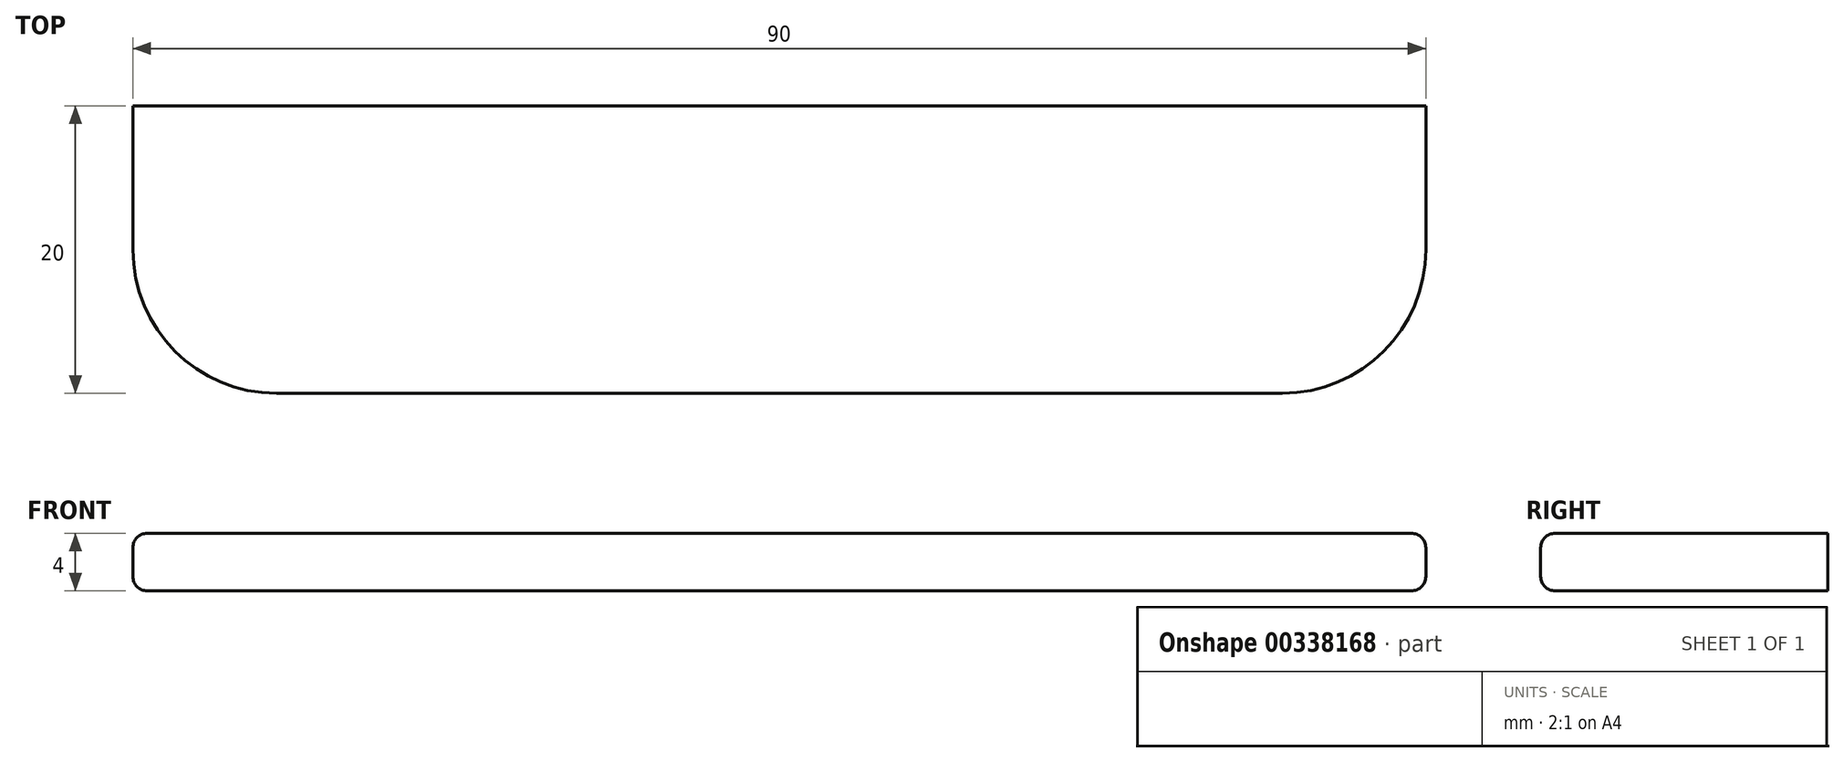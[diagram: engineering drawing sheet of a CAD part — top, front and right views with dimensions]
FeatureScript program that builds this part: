
annotation { "Feature Type Name" : "Feature", "Feature Type Description" : "" }
export const myFeature = defineFeature(function(context is Context, id is Id, definition is map)
    precondition{}
    {
        {
            var Q0;
            Q0=qCreatedBy(makeId("Top.planeOp"),FACE);
            var sketch = newSketch(context, id + "F0", { "sketchPlane" : qUnion([Q0])});
            skLineSegment(sketch, "E0.bottom", {"start": v(-45, 0) * mm, "end": v(45, 0) * mm});
            skLineSegment(sketch, "E0.top", {"start": v(-35, -20) * mm, "end": v(35, -20) * mm});
            skLineSegment(sketch, "E0.left", {"start": v(-45, 0) * mm, "end": v(-45, -10) * mm});
            skLineSegment(sketch, "E0.right", {"start": v(45, 0) * mm, "end": v(45, -10) * mm});
            skPoint(sketch, "E1.visualSharp", {"position": v(-45, -20) * mm});
            skArc(sketch, "E1.filletArc", {"start": v(-45, -10) * mm, "mid": v(-42.07, -17.07) * mm, "end": v(-35, -20) * mm});
            skPoint(sketch, "E2.visualSharp", {"position": v(45, -20) * mm});
            skArc(sketch, "E2.filletArc", {"start": v(35, -20) * mm, "mid": v(42.07, -17.07) * mm, "end": v(45, -10) * mm});
            skPoint(sketch, "E3", {"position": v(0, 0) * mm});
            skLineSegment(sketch, "E4", {"start": v(0, 0) * mm, "end": v(0, -20) * mm, "construction": true});
            skSolve(sketch);
        }
        {
            var Q0;
            Q0=makeQuery(id+"F0.imprint","IMPRINT",FACE,{"disambiguationData":[TD([[makeQuery(id+"F0.imprint","IMPRINT",EDGE,{"derivedFrom":sQuery(id+"F0.wireOp",EDGE,"E0.bottom")}),-1.0]])]});
            var Q1;
            Q1=sQuery(id+"F0.wireOp",EDGE,"E1.filletArc");
            var Q2;
            Q2=sQuery(id+"F0.wireOp",EDGE,"E0.bottom");
            var Q3;
            Q3=sQuery(id+"F0.wireOp",EDGE,"E0.left");
            extrude(context, id + "F1", {"entities" : qUnion([Q0]), "surfaceEntities" : qUnion([Q1, Q2, Q3]), "depth" : 4 * mm});
        }
        {
            var Q0;
            Q0=makeQuery(id+"F1.opExtrude","CAP_EDGE",EDGE,{"disambiguationData":[OSD([sQuery(id+"F0.wireOp",EDGE,"E0.left")])],"isStart":false});
            var Q1;
            Q1=makeQuery(id+"F1.opExtrude","CAP_EDGE",EDGE,{"disambiguationData":[OSD([sQuery(id+"F0.wireOp",EDGE,"E1.filletArc")])],"isStart":true});
            fillet(context, id + "F2", {"entities" : qUnion([Q0, Q1]), "radius" : 1 * mm, "tangentPropagation" : true, "allowEdgeOverflow" : false});
        }
    });
